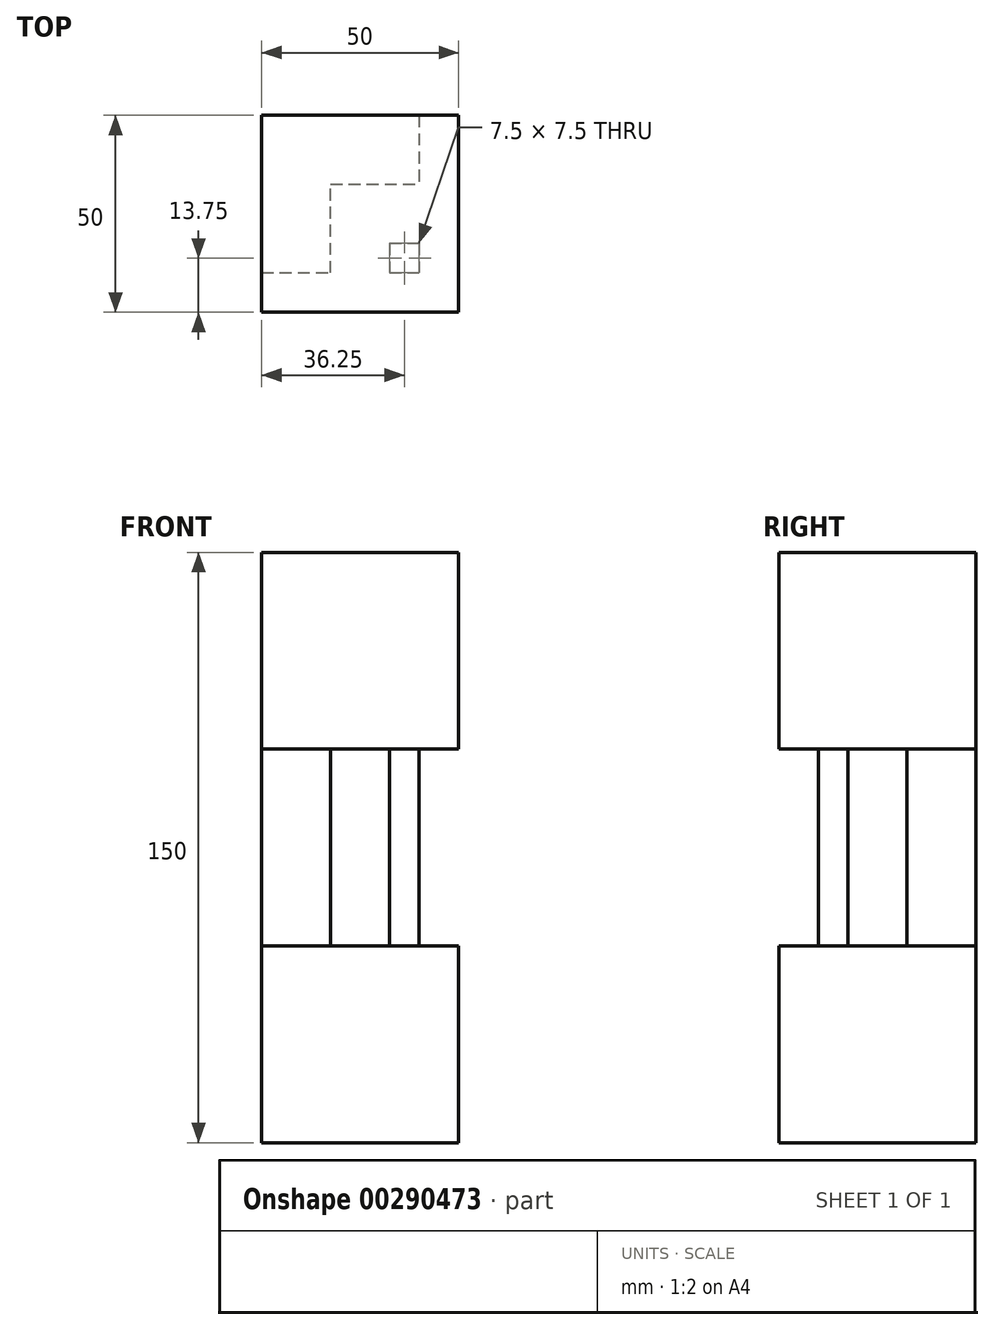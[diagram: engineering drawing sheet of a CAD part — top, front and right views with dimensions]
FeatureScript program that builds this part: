
annotation { "Feature Type Name" : "Feature", "Feature Type Description" : "" }
export const myFeature = defineFeature(function(context is Context, id is Id, definition is map)
    precondition{}
    {
        {
            var Q0;
            Q0=qCreatedBy(makeId("Top.planeOp"),FACE);
            var sketch = newSketch(context, id + "F0", { "sketchPlane" : qUnion([Q0])});
            skLineSegment(sketch, "E0.bottom", {"start": v(25, 25) * mm, "end": v(-25, 25) * mm});
            skLineSegment(sketch, "E0.top", {"start": v(25, -25) * mm, "end": v(-25, -25) * mm});
            skLineSegment(sketch, "E0.left", {"start": v(25, 25) * mm, "end": v(25, -25) * mm});
            skLineSegment(sketch, "E0.right", {"start": v(-25, 25) * mm, "end": v(-25, -25) * mm});
            skPoint(sketch, "E0.middle", {"position": v(0, 0) * mm});
            skSolve(sketch);
        }
        {
            var Q0;
            Q0 = qSketchRegion(id + "F0", true);
            extrude(context, id + "F1", {"entities" : qUnion([Q0]), "depth" : 50 * mm});
        }
        {
            var Q0;
            Q0=makeQuery(id+"F1.opExtrude","CAP_FACE",FACE,{"disambiguationData":[OSD([sQuery(id+"F0.wireOp",EDGE,"E0.bottom"),sQuery(id+"F0.wireOp",EDGE,"E0.top"),sQuery(id+"F0.wireOp",EDGE,"E0.left"),sQuery(id+"F0.wireOp",EDGE,"E0.right")])],"isStart":false});
            var sketch = newSketch(context, id + "F2", { "sketchPlane" : qUnion([Q0])});
            skLineSegment(sketch, "E1.bottom", {"start": v(-25, 25) * mm, "end": v(15, 25) * mm});
            skLineSegment(sketch, "E1.left", {"start": v(-25, 25) * mm, "end": v(-25, -15) * mm});
            skLineSegment(sketch, "E2.top", {"start": v(-25, -15) * mm, "end": v(-7.5, -15) * mm});
            skLineSegment(sketch, "E3.top", {"start": v(-7.5, 7.5) * mm, "end": v(15, 7.5) * mm});
            skLineSegment(sketch, "E3.right", {"start": v(15, 25) * mm, "end": v(15, 7.5) * mm});
            skLineSegment(sketch, "E4.bottom", {"start": v(7.5, -7.5) * mm, "end": v(15, -7.5) * mm});
            skLineSegment(sketch, "E4.top", {"start": v(7.5, -15) * mm, "end": v(15, -15) * mm});
            skLineSegment(sketch, "E4.left", {"start": v(7.5, -7.5) * mm, "end": v(7.5, -15) * mm});
            skLineSegment(sketch, "E4.right", {"start": v(15, -7.5) * mm, "end": v(15, -15) * mm});
            skLineSegment(sketch, "E5", {"start": v(-7.5, -15) * mm, "end": v(-7.5, 7.5) * mm});
            skLineSegment(sketch, "E6", {"start": v(0, -25) * mm, "end": v(0, 25) * mm, "construction": true});
            skLineSegment(sketch, "E7", {"start": v(25, 0) * mm, "end": v(-25, 0) * mm, "construction": true});
            skSolve(sketch);
        }
        {
            var Q0;
            Q0 = qSketchRegion(id + "F2", true);
            extrude(context, id + "F3", {"entities" : qUnion([Q0]), "operationType" : NewBodyOperationType.ADD, "depth" : 50 * mm});
        }
        {
            var Q0;
            Q0=makeQuery(id+"F3.opExtrude","CAP_FACE",FACE,{"disambiguationData":[OSD([sQuery(id+"F2.wireOp",EDGE,"E1.bottom"),sQuery(id+"F2.wireOp",EDGE,"E1.top"),sQuery(id+"F2.wireOp",EDGE,"E1.left"),sQuery(id+"F2.wireOp",EDGE,"E1.right")])],"isStart":false});
            var sketch = newSketch(context, id + "F4", { "sketchPlane" : qUnion([Q0])});
            skLineSegment(sketch, "E8.bottom", {"start": v(-25, 25) * mm, "end": v(25, 25) * mm});
            skLineSegment(sketch, "E8.top", {"start": v(-25, -25) * mm, "end": v(25, -25) * mm});
            skLineSegment(sketch, "E8.left", {"start": v(-25, 25) * mm, "end": v(-25, -25) * mm});
            skLineSegment(sketch, "E8.right", {"start": v(25, 25) * mm, "end": v(25, -25) * mm});
            skSolve(sketch);
        }
        {
            var Q0;
            Q0 = qSketchRegion(id + "F4", true);
            extrude(context, id + "F5", {"entities" : qUnion([Q0]), "operationType" : NewBodyOperationType.ADD, "depth" : 50 * mm});
        }
    });
